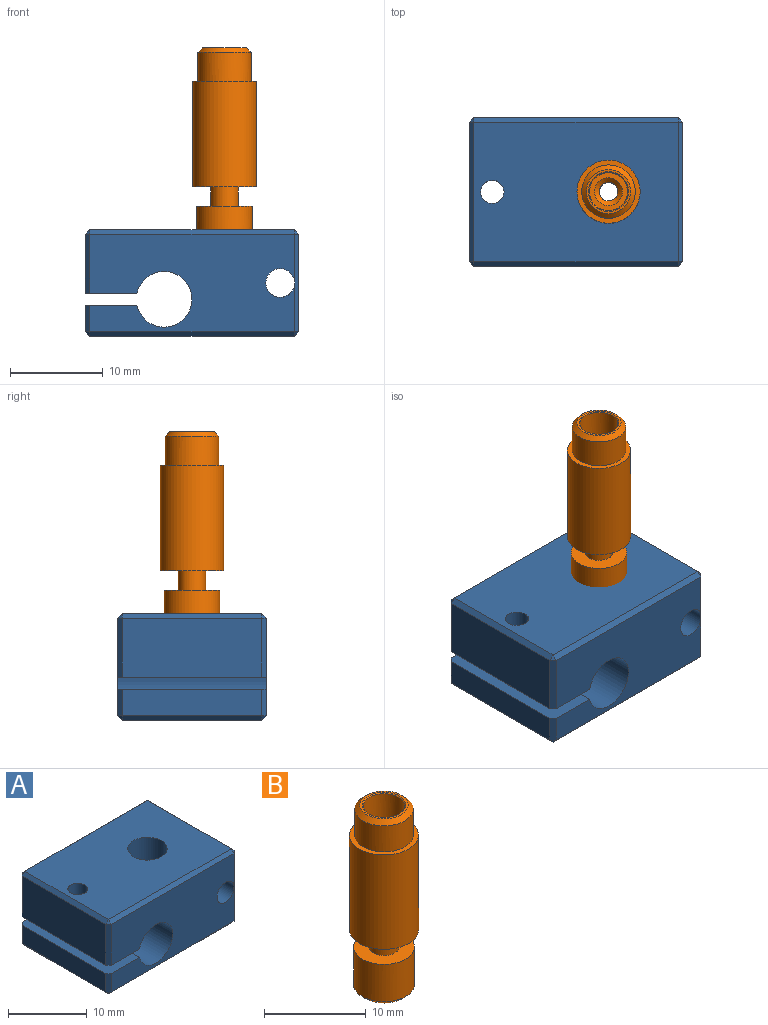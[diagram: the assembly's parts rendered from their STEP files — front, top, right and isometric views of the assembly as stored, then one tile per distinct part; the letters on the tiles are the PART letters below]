
ASSEMBLY  parts=2 mates=1
PART A: 37 faces, bbox 23x16x11.5 mm
  f0: cylinder r=1.55mm len=16mm, axis (0,-1,0), area 150.3mm2, adj f2,f4,f14,f25,f36
  f1: plane 15x2.85mm, normal (-1,0,0), area 42.8mm2, adj f8,f16,f22,f23
  f2: plane 22x10.5mm, normal (0,1,0), area 188.7mm2, adj f0,f8,f9,f10,f21,f22,f31,f32
  f3: plane 15x6.35mm, normal (-1,0,0), area 95.2mm2, adj f10,f15,f20,f21
  f4: plane 22x10.5mm, normal (0,-1,0), area 188.7mm2, adj f0,f8,f9,f10,f15,f16,f19,f24
  f5: plane 15x10.5mm, normal (1,0,0), area 157.5mm2, adj f25,f30,f33,f36
  f6: plane 22x15mm, normal (0,0,1), area 305.5mm2, adj f11,f12,f19,f20,f30,f31
  f7: plane 22x15mm, normal (0,0,-1), area 300.5mm2, adj f11,f13,f14,f23,f24,f32,f33
  f8: plane 16x5.57mm, normal (0,0,1), area 84mm2, adj f1,f2,f4,f9,f13,f16,f22
  f9: cylinder r=3mm len=16mm, axis (0,-1,0), area 280.6mm2, adj f2,f4,f8,f10
  f10: plane 16x5.57mm, normal (0,0,-1), area 84mm2, adj f2,f3,f4,f9,f12,f15,f21
  f11: cylinder r=2.5mm len=11.5mm, axis (0,0,1), area 180.6mm2, adj f6,f7
  f12: cylinder r=1.25mm len=6.85mm, axis (0,0,1), area 53.8mm2, adj f6,f10
  f13: cylinder r=1.25mm len=3.35mm, axis (0,0,1), area 26.3mm2, adj f7,f8
  f14: cylinder r=1.25mm len=4.83mm, axis (0,0,-1), area 35.3mm2, adj f0,f7
  f15: plane 6.35x0.5mm, normal (-0.71,-0.71,0), area 4.5mm2, adj f3,f4,f10,f17
  f16: plane 2.85x0.5mm, normal (-0.71,-0.71,0), area 2mm2, adj f1,f4,f8,f18
  f17: plane 0.5x0.5mm, normal (-0.58,-0.58,0.58), area 0.2mm2, adj f15,f19,f20
  f18: plane 0.5x0.5mm, normal (-0.58,-0.58,-0.58), area 0.2mm2, adj f16,f23,f24
  f19: plane 22x0.5mm, normal (0,-0.71,0.71), area 15.6mm2, adj f4,f6,f17,f26
  f20: plane 15x0.5mm, normal (-0.71,0,0.71), area 10.6mm2, adj f3,f6,f17,f27
  f21: plane 6.35x0.5mm, normal (-0.71,0.71,0), area 4.5mm2, adj f2,f3,f10,f27
  f22: plane 2.85x0.5mm, normal (-0.71,0.71,0), area 2mm2, adj f1,f2,f8,f28
  f23: plane 15x0.5mm, normal (-0.71,0,-0.71), area 10.6mm2, adj f1,f7,f18,f28
  f24: plane 22x0.5mm, normal (0,-0.71,-0.71), area 15.6mm2, adj f4,f7,f18,f29
  f25: plane 10.5x0.5mm, normal (0.71,-0.71,0), area 7.4mm2, adj f0,f4,f5,f26,f29
  f26: plane 0.5x0.5mm, normal (0.58,-0.58,0.58), area 0.2mm2, adj f19,f25,f30
  f27: plane 0.5x0.5mm, normal (-0.58,0.58,0.58), area 0.2mm2, adj f20,f21,f31
  f28: plane 0.5x0.5mm, normal (-0.58,0.58,-0.58), area 0.2mm2, adj f22,f23,f32
  f29: plane 0.5x0.5mm, normal (0.58,-0.58,-0.58), area 0.2mm2, adj f24,f25,f33
  f30: plane 15x0.5mm, normal (0.71,0,0.71), area 10.6mm2, adj f5,f6,f26,f34
  f31: plane 22x0.5mm, normal (0,0.71,0.71), area 15.6mm2, adj f2,f6,f27,f34
  f32: plane 22x0.5mm, normal (0,0.71,-0.71), area 15.6mm2, adj f2,f7,f28,f35
  f33: plane 15x0.5mm, normal (0.71,0,-0.71), area 10.6mm2, adj f5,f7,f29,f35
  f34: plane 0.5x0.5mm, normal (0.58,0.58,0.58), area 0.2mm2, adj f30,f31,f36
  f35: plane 0.5x0.5mm, normal (0.58,0.58,-0.58), area 0.2mm2, adj f32,f33,f36
  f36: plane 10.5x0.5mm, normal (0.71,0.71,0), area 7.4mm2, adj f0,f2,f5,f34,f35
PART B: 17 faces, bbox 6.8x6.8x22.1 mm
  f0: cylinder r=2.88mm len=5.75mm, axis (0,0,-1), area 56.5mm2, adj f11,f12
  f1: plane 4.75x4.75mm, normal (0,0,1), area 3.2mm2, adj f12,f14
  f2: cylinder r=2.05mm len=4.1mm, axis (0,0,-1), area 45.5mm2, adj f3,f14
  f3: plane 4.1x4.1mm, normal (0,0,1), area 6.1mm2, adj f2,f16
  f4: cylinder r=1mm len=17.87mm, axis (0,0,-1), area 112.3mm2, adj f15,f16
  f5: plane 5x5mm, normal (0,0,-1), area 15.8mm2, adj f13,f15
  f6: cylinder r=3mm len=6mm, axis (0,0,-1), area 84.8mm2, adj f7,f13
  f7: plane 6x6mm, normal (0,0,1), area 21.4mm2, adj f6,f8
  f8: cylinder r=1.48mm len=2.96mm, axis (0,0,-1), area 19.5mm2, adj f7,f9
  f9: plane 6.8x6.8mm, normal (0,0,-1), area 29.4mm2, adj f8,f10
  f10: cylinder r=3.4mm len=11.37mm, axis (0,0,-1), area 242.9mm2, adj f9,f11
  f11: plane 6.8x6.8mm, normal (0,0,1), area 10.3mm2, adj f0,f10
  f12: cone r=2.88mm half-angle=45deg, axis (0,0,-1), area 11.7mm2, adj f0,f1
  f13: cone r=2.5mm half-angle=45deg, axis (0,0,1), area 12.2mm2, adj f5,f6
  f14: cone r=2.15mm half-angle=45deg, axis (0,0,1), area 1.9mm2, adj f1,f2
  f15: cone r=1mm half-angle=45deg, axis (0,0,-1), area 0.9mm2, adj f4,f5
  f16: cone r=1.5mm half-angle=45deg, axis (0,0,1), area 5.6mm2, adj f3,f4
PLACE A t=(0.1,-0.1,0.85)mm
PLACE B t=(-7.9,7.9,16.95)mm
MATE fastened B.f0 <-> A.f11  axis (0,0,-1) through (-7.9,7.9,9.85)mm
